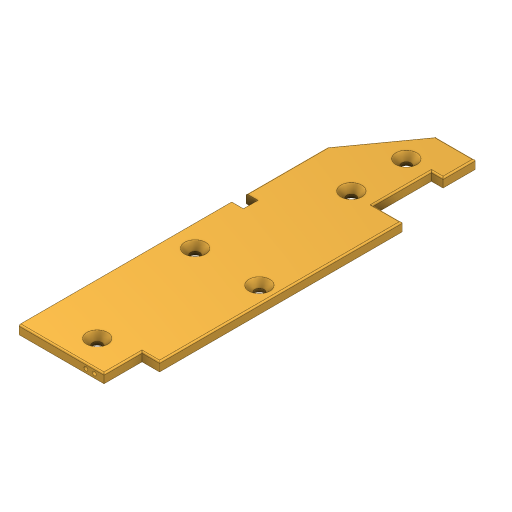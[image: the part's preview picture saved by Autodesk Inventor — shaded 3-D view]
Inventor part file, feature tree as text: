
AUTODESK INVENTOR PART (.ipt)
format: ipt  version: 2024.3 (Build 283343000, 343)  size: 1,328,640 bytes
history: native  units: mm
features: extrude x34, chamfer x24, fillet x18, sketch x10, other x3, projected_geometry x2, pattern_linear x1
ambient origin geometry x8: Origin, YZ Plane, XZ Plane, XY Plane, X Axis, Y Axis, Z Axis, Center Point
bodies: Solid1 (feature_tree)
feature tree (92):
  other  "Table"
  other  "Upside"
  other  "Downside"
  sketch  "Sketch1"  dims[d4=12.5mm d5=4.0mm]
  extrude  "Extrusion1"  Depth=4.0mm
  extrude  "Extrusion2"  Depth=34.1mm
  extrude  "Extrusion3"  Depth=1.5mm
  extrude  "Extrusion4"  Depth=0.5mm
  extrude  "Extrusion5"  Depth=1.5mm
  extrude  "Extrusion6"  Depth=1.5mm
  extrude  "Extrusion7"  Depth=1.0mm
  extrude  "Extrusion27"  Depth=0.5mm
  extrude  "Extrusion41"  Depth=0.5mm TaperAngle=0.0deg
  extrude  "Extrusion42"  Depth=0.5mm TaperAngle=0.0deg
  extrude  "Extrusion43"  Depth=1.0mm
  chamfer  "Chamfer16"  Distance=2.0mm
  chamfer  "Chamfer17"  Distance=111.0mm
  chamfer  "Chamfer18"  Distance=16.0mm
  chamfer  "Chamfer19"  Distance=5.0mm
  chamfer  "Chamfer20"  Distance=33.6mm
  chamfer  "Chamfer21"  Distance=10.6mm
  chamfer  "Chamfer22"  Distance=33.6mm
  chamfer  "Chamfer23"  Distance=5.0mm
  fillet  "Fillet17"  Radius=6.0mm
  extrude  "Extrusion8"  Depth=0.5mm
  extrude  "Extrusion9"  Depth=0.5mm
  extrude  "Extrusion10"  Depth=0.5mm TaperAngle=0.0deg
  extrude  "Extrusion11"  Depth=0.5mm TaperAngle=0.0deg
  chamfer  "Chamfer6"  Distance=3.1mm
  sketch  "Sketch Driven Pattern1"  dims[d6=11.2mm d7=34.1mm]
  fillet  "Fillet2"  Radius=5.0mm
  fillet  "Fillet3"  Radius=6.0mm
  extrude  "Extrusion26"  Depth=4.0mm
  chamfer  "Chamfer3"  Distance=5.0mm
  extrude  "Extrusion32"  Depth=0.5mm TaperAngle=0.0deg
  extrude  "Extrusion30"  TaperAngle=0.0deg  [1 undecoded]
  extrude  "Extrusion12"  Depth=0.5mm TaperAngle=0.0deg
  extrude  "Extrusion15"  Depth=2.0mm TaperAngle=0.0deg
  extrude  "Extrusion13"  Depth=0.5mm TaperAngle=0.0deg
  extrude  "Extrusion36"  Depth=4.0mm TaperAngle=0.0deg
  extrude  "Extrusion37"  Depth=0.5mm TaperAngle=0.0deg
  extrude  "Extrusion29"  Depth=5.0mm TaperAngle=0.0deg
  extrude  "Extrusion19"  Depth=2.0mm TaperAngle=45.0deg
  extrude  "Extrusion20"  Depth=1.0mm TaperAngle=45.0deg
  extrude  "Extrusion21"  Depth=2.0mm
  extrude  "Extrusion22"  Depth=4.25mm TaperAngle=0.0deg
  chamfer  "Chamfer2"  Distance=1.0mm
  chamfer  "Chamfer1"  Distance=80.0mm
  extrude  "Extrusion39"  Depth=2.0mm
  extrude  "Extrusion40"  Depth=0.3mm
  chamfer  "Chamfer9"  Distance=1.0mm
  chamfer  "Chamfer10"  Distance=1.5mm
  chamfer  "Chamfer11"  Distance=1.5mm
  chamfer  "Chamfer8"  Distance=1.5mm
  fillet  "Fillet16"  Radius=0.5mm
  chamfer  "Chamfer12"  Distance=0.5mm
  chamfer  "Chamfer13"  Distance=1.5mm
  chamfer  "Chamfer14"  Distance=32.0mm
  chamfer  "Chamfer15"  Distance=0.5mm
  sketch  "Sketch Driven Pattern2"  dims[d9=1.5mm d10=1.5mm]
  extrude  "Extrusion23"  Depth=0.5mm
  fillet  "Fillet1"  Radius=5.0mm
  pattern_linear  "Rectangular Pattern1"  Spacing1=5.0mm  [1 undecoded]
  fillet  "Fillet4"  Radius=5.0mm
  fillet  "Fillet5"  Radius=0.5mm
  chamfer  "Chamfer4"  Distance=0.5mm
  extrude  "Extrusion33"  Depth=0.5mm
  chamfer  "Chamfer7"  Distance=1.5mm
  fillet  "Fillet8"  Radius=0.5mm
  fillet  "Fillet9"  Radius=0.5mm
  fillet  "Fillet15"  Radius=0.5mm
  fillet  "Fillet10"  Radius=1.5mm
  fillet  "Fillet12"  Radius=11.0mm
  fillet  "Fillet13"  Radius=1.5mm
  fillet  "Fillet14"  Radius=0.5mm
  sketch  "Sketch8"  dims[d49=0.5mm d54=0.5mm]
  extrude  "Extrusion34"  Depth=1.5mm
  extrude  "Extrusion35"  Depth=1.0mm
  fillet  "Fillet6"  Radius=1.5mm
  fillet  "Fillet7"  Radius=0.5mm
  sketch  "Sketch Driven Pattern3"  dims[d14=0.5mm d18=1.5mm]
  fillet  "Fillet11"  Radius=1.0mm
  chamfer  "Chamfer24"  Distance=1.0mm
  chamfer  "Chamfer25"  Distance=3.0mm
  fillet  "Fillet18"  Radius=1.0mm
  sketch  "Sketch2"  dims[d12=0.5mm d13=0.5mm]
  sketch  "Sketch3"  dims[d20=1.5mm d21=1.5mm]
  sketch  "Sketch5"  dims[d23=25.0mm]
  projected_geometry  "Projected Loop1"
  sketch  "Sketch7"  dims[d24=11.2mm d25=34.1mm d26=1.5mm d27=1.5mm d30=0.5mm d31=0.5mm d35=1.5mm d36=1.0mm d37=25.0mm d40=1.0mm]
  projected_geometry  "Projected Loop3"
  sketch  "Sketch9"  dims[d55=7.0mm d56=0.0mm d57=6.0mm d58=0.0mm d59=3.5mm d60=0.0mm d61=1.0mm d62=2.0mm d63=0.0mm d64=111.0mm d65=16.0mm d68=5.0mm d69=0.0mm d72=33.6mm d73=10.6mm d74=33.6mm d75=5.0mm d76=0.0mm d77=6.0mm d78=0.0mm d79=0.5mm d80=0.5mm d81=0.7mm d82=0.0mm d87=7.0mm d88=0.0mm d91=3.1mm d92=5.0mm d93=0.0mm d94=6.0mm d95=4.0mm d96=5.0mm d97=0.7mm d98=0.0mm d100=0.0mm d101=2.25mm d102=0.0mm d105=2.0mm d106=0.0mm d113=0.5mm d114=0.0mm d115=4.0mm d116=0.0mm d117=0.5mm d118=0.0mm d119=5.0mm d120=0.0mm d121=2.0mm d122=2.0mm d123=45.0deg d124=1.0mm d125=2.0mm d126=45.0deg d127=2.0mm d129=14.5mm d130=4.25mm d131=0.0mm d132=0.0mm d133=1.0mm d134=80.0mm d136=3.27mm d137=2.0mm d139=0.3mm d140=1.0mm d148=1.5mm d149=1.5mm d150=1.5mm d151=0.5mm d152=0.5mm d153=1.5mm d154=32.0mm d156=20.0mm d159=0.5mm d161=0.5mm d162=5.0mm d165=5.0mm d166=5.0mm d167=0.0mm d168=0.5mm d169=0.5mm d170=0.5mm d171=1.5mm d172=0.5mm d173=0.5mm d174=0.5mm d175=1.5mm d176=11.0mm d177=1.5mm d178=0.5mm d179=1.5mm d180=1.0mm d181=1.5mm d182=0.5mm d185=1.0mm d186=1.0mm d187=3.0mm d188=1.0mm d189=1.0mm d190=3.7mm d191=0.0mm d192=1.5mm d193=0.5mm d194=0.5mm d195=0.5mm d196=0.5mm d197=0.5mm d198=0.5mm d199=1.5mm d200=1.5mm d201=15.0mm d202=13.0mm d203=6.0mm d207=1.0mm d208=0.0mm d209=0.25mm d210=2.0mm d211=45.0deg d212=0.25mm d213=2.0mm d214=45.0deg d232=3.0mm d235=0.0mm d236=1.8mm d237=1.8mm d246=4.0mm d247=0.0mm d250=0.65mm d251=0.0mm d252=1.8mm d254=7.25mm d255=0.0mm d256=7.25mm d257=0.0mm d261=6.5mm d262=2.0mm d263=0.0mm d264=0.5mm d265=0.0mm d266=1.0mm d267=0.2mm d268=1.0mm d269=1.2mm d270=1.2mm d271=3.0mm d276=0.0mm d277=1.0mm d278=0.0mm d279=0.25mm d280=1.0mm d281=2.0mm d282=45.0deg d283=0.1mm d284=2.0mm d285=45.0deg d286=0.2mm d287=0.5mm d288=0.5mm d289=0.5mm d290=0.5mm d291=0.5mm d292=0.5mm d293=0.5mm d294=106.0mm d295=0.5mm d296=0.5mm d297=0.5mm d298=0.5mm d299=0.5mm d300=0.5mm d303=1.0mm d304=5.0mm d305=1.5mm d306=1.5mm d308=1.5mm d309=0.5mm d310=31.0mm d311=4.0mm d312=11.5mm d313=30.25mm d316=0.5mm d318=1.5mm d319=0.5mm d320=1.0mm d321=10.0mm d322=0.5mm d323=1.5mm d324=0.5mm d325=4.0mm d326=2.0mm d327=2.0mm d329=0.3mm d330=0.3mm d333=2.3mm d334=0.0mm d335=1.3mm d336=0.0mm d337=0.3mm d338=0.8mm d339=45.0deg d340=0.125mm d341=0.3mm d342=0.8mm d343=45.0deg d344=0.3mm d345=0.8mm d346=45.0deg d347=0.3mm d348=0.8mm d349=45.0deg d350=0.3mm d351=2.0mm d352=45.0deg d353=0.3mm d354=2.0mm d355=45.0deg d356=0.3mm d357=2.0mm d358=45.0deg d359=0.3mm d360=2.0mm d361=45.0deg d362=3.7mm d363=0.0mm d364=2.7mm d365=0.0mm d366=4.7mm d367=0.0mm d368=2.0mm d369=0.3mm d370=45.0deg d371=2.0mm d372=0.3mm d373=45.0deg d374=2.0mm d375=0.3mm d376=45.0deg d377=2.0mm d378=0.3mm d379=45.0deg d380=0.8mm d381=0.3mm d382=45.0deg d383=0.8mm d384=0.3mm d385=45.0deg d386=0.8mm d387=0.3mm d388=45.0deg d389=0.8mm d390=0.3mm d391=45.0deg d392=0.125mm d393=0.3mm d394=0.3mm d395=45.0deg d396=0.3mm d397=0.3mm d398=45.0deg d399=150.0mm d401=5.0mm d402=10.0mm d404=10.0mm d407=1.5mm d408=60.0mm d410=5.2mm d411=10.0mm d413=10.0mm d415=0.5mm d142=0.5mm d143=0.872665mm d144=0.5mm d145=0.872665mm d328=0.5mm]
note: 2 required parameter values undecoded (feature->parameter linkage not recoverable at this tier; creation-order binding heuristic only, values carry confidence <= 0.55)
